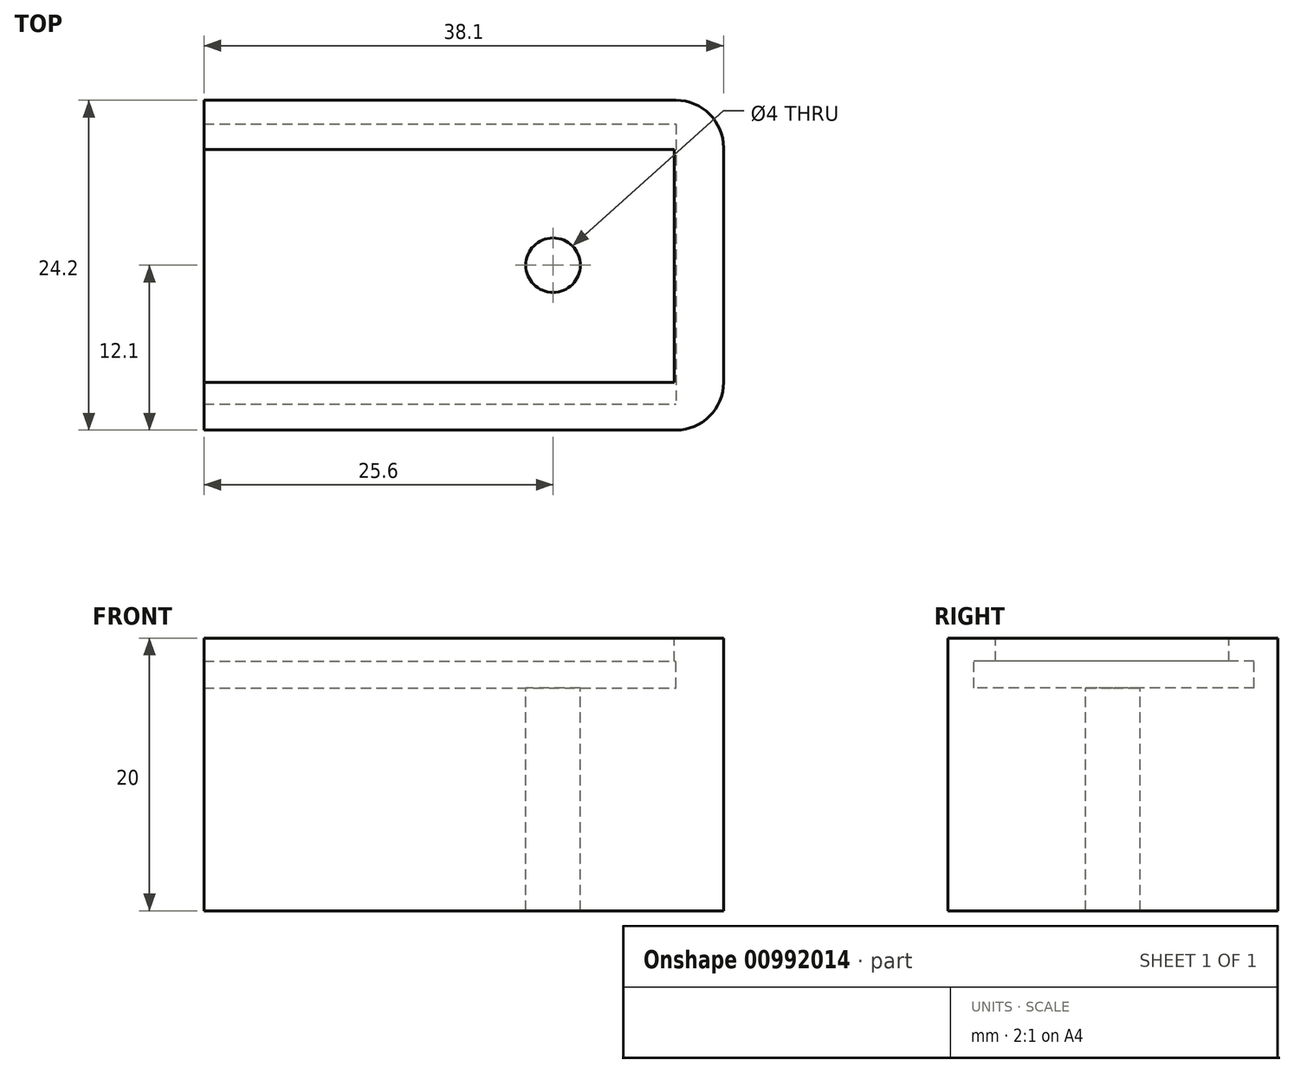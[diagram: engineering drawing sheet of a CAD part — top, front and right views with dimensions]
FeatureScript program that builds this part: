
annotation { "Feature Type Name" : "Feature", "Feature Type Description" : "" }
export const myFeature = defineFeature(function(context is Context, id is Id, definition is map)
    precondition{}
    {
        {
            var Q0;
            Q0=qCreatedBy(makeId("Top.planeOp"),FACE);
            var sketch = newSketch(context, id + "F0", { "sketchPlane" : qUnion([Q0])});
            skLineSegment(sketch, "E0.bottom", {"start": v(0, 0) * mm, "end": v(-38.1, 0) * mm});
            skLineSegment(sketch, "E0.top", {"start": v(0, 24.2) * mm, "end": v(-38.1, 24.2) * mm});
            skLineSegment(sketch, "E0.left", {"start": v(0, 0) * mm, "end": v(0, 24.2) * mm});
            skLineSegment(sketch, "E0.right", {"start": v(-38.1, 0) * mm, "end": v(-38.1, 24.2) * mm});
            skSolve(sketch);
        }
        {
            var Q0;
            Q0 = qSketchRegion(id + "F0", true);
            extrude(context, id + "F1", {"entities" : qUnion([Q0]), "depth" : 20 * mm, "offsetDistance" : 25 * mm});
        }
        {
            var Q0;
            Q0=makeQuery(id+"F1.opExtrude","CAP_FACE",FACE,{"disambiguationData":[OSD([sQuery(id+"F0.wireOp",EDGE,"E0.bottom"),sQuery(id+"F0.wireOp",EDGE,"E0.top"),sQuery(id+"F0.wireOp",EDGE,"E0.left"),sQuery(id+"F0.wireOp",EDGE,"E0.right")])],"isStart":false});
            var sketch = newSketch(context, id + "F2", { "sketchPlane" : qUnion([Q0])});
            skLineSegment(sketch, "E1.bottom", {"start": v(-38.1, 20.6) * mm, "end": v(-3.6, 20.6) * mm});
            skLineSegment(sketch, "E1.top", {"start": v(-38.1, 3.5) * mm, "end": v(-3.6, 3.5) * mm});
            skLineSegment(sketch, "E1.left", {"start": v(-38.1, 20.6) * mm, "end": v(-38.1, 3.5) * mm});
            skLineSegment(sketch, "E1.right", {"start": v(-3.6, 20.6) * mm, "end": v(-3.6, 3.5) * mm});
            skSolve(sketch);
        }
        {
            var Q0;
            Q0=makeQuery(id+"F2.imprint","IMPRINT",FACE,{"disambiguationData":[TD([[makeQuery(id+"F2.imprint","IMPRINT",EDGE,{"derivedFrom":sQuery(id+"F2.wireOp",EDGE,"E1.bottom")}),-1.0]])]});
            extrude(context, id + "F3", {"entities" : qUnion([Q0]), "operationType" : NewBodyOperationType.REMOVE, "oppositeDirection" : true, "depth" : 1.7 * mm, "offsetDistance" : 25 * mm});
        }
        {
            var Q0;
            Q0=makeQuery(id+"F3.boolean.opBoolean","COPY",FACE,{"derivedFrom":makeQuery(id+"F3.opExtrude","CAP_FACE",FACE,{"disambiguationData":[OSD([sQuery(id+"F2.wireOp",EDGE,"E1.bottom"),sQuery(id+"F2.wireOp",EDGE,"E1.top"),sQuery(id+"F2.wireOp",EDGE,"E1.left"),sQuery(id+"F2.wireOp",EDGE,"E1.right")])],"isStart":false})});
            var sketch = newSketch(context, id + "F4", { "sketchPlane" : qUnion([Q0])});
            skLineSegment(sketch, "E2.bottom", {"start": v(-38.1, 22.46) * mm, "end": v(-3.5, 22.46) * mm});
            skLineSegment(sketch, "E2.top", {"start": v(-38.1, 1.9) * mm, "end": v(-3.5, 1.9) * mm});
            skLineSegment(sketch, "E2.left", {"start": v(-38.1, 22.46) * mm, "end": v(-38.1, 1.9) * mm});
            skLineSegment(sketch, "E2.right", {"start": v(-3.5, 22.46) * mm, "end": v(-3.5, 1.9) * mm});
            skSolve(sketch);
        }
        {
            var Q0;
            Q0 = qSketchRegion(id + "F4", true);
            extrude(context, id + "F5", {"entities" : qUnion([Q0]), "operationType" : NewBodyOperationType.REMOVE, "oppositeDirection" : true, "depth" : 1.95 * mm, "offsetDistance" : 25 * mm});
        }
        {
            var Q0;
            Q0=makeQuery(id+"F1.opExtrude","SWEPT_EDGE",EDGE,{"disambiguationData":[OSD([sQuery(id+"F0.wireOp",EDGE,"E0.top"),sQuery(id+"F0.wireOp",EDGE,"E0.left")])]});
            var Q1;
            Q1=makeQuery(id+"F1.opExtrude","SWEPT_EDGE",EDGE,{"disambiguationData":[OSD([sQuery(id+"F0.wireOp",EDGE,"E0.bottom"),sQuery(id+"F0.wireOp",EDGE,"E0.left")])]});
            fillet(context, id + "F6", {"entities" : qUnion([Q0, Q1]), "radius" : 3.5 * mm, "tangentPropagation" : true, "allowEdgeOverflow" : false});
        }
        {
            var Q0;
            Q0=makeQuery(id+"F5.boolean.opBoolean","COPY",FACE,{"derivedFrom":makeQuery(id+"F5.opExtrude","CAP_FACE",FACE,{"disambiguationData":[OSD([sQuery(id+"F4.wireOp",EDGE,"E2.bottom"),sQuery(id+"F4.wireOp",EDGE,"E2.top"),sQuery(id+"F4.wireOp",EDGE,"E2.left"),sQuery(id+"F4.wireOp",EDGE,"E2.right")])],"isStart":false})});
            var sketch = newSketch(context, id + "F7", { "sketchPlane" : qUnion([Q0])});
            skCircle(sketch, "E3", {"center": v(-12.5, 12.1) * mm, "radius": 2 * mm});
            skSolve(sketch);
        }
        {
            var Q0;
            Q0 = qSketchRegion(id + "F7", true);
            var Q1;
            Q1=makeQuery(id+"F1.opExtrude","SWEPT_BODY",BODY,{"disambiguationData":[OSD([sQuery(id+"F0.wireOp",EDGE,"E0.bottom"),sQuery(id+"F0.wireOp",EDGE,"E0.top"),sQuery(id+"F0.wireOp",EDGE,"E0.left"),sQuery(id+"F0.wireOp",EDGE,"E0.right")])]});
            extrude(context, id + "F8", {"entities" : qUnion([Q0]), "operationType" : NewBodyOperationType.REMOVE, "endBound" : BoundingType.UP_TO_BODY, "oppositeDirection" : true, "depth" : 25 * mm, "endBoundEntityBody" : qUnion([Q1]), "offsetDistance" : 25 * mm});
        }
    });
